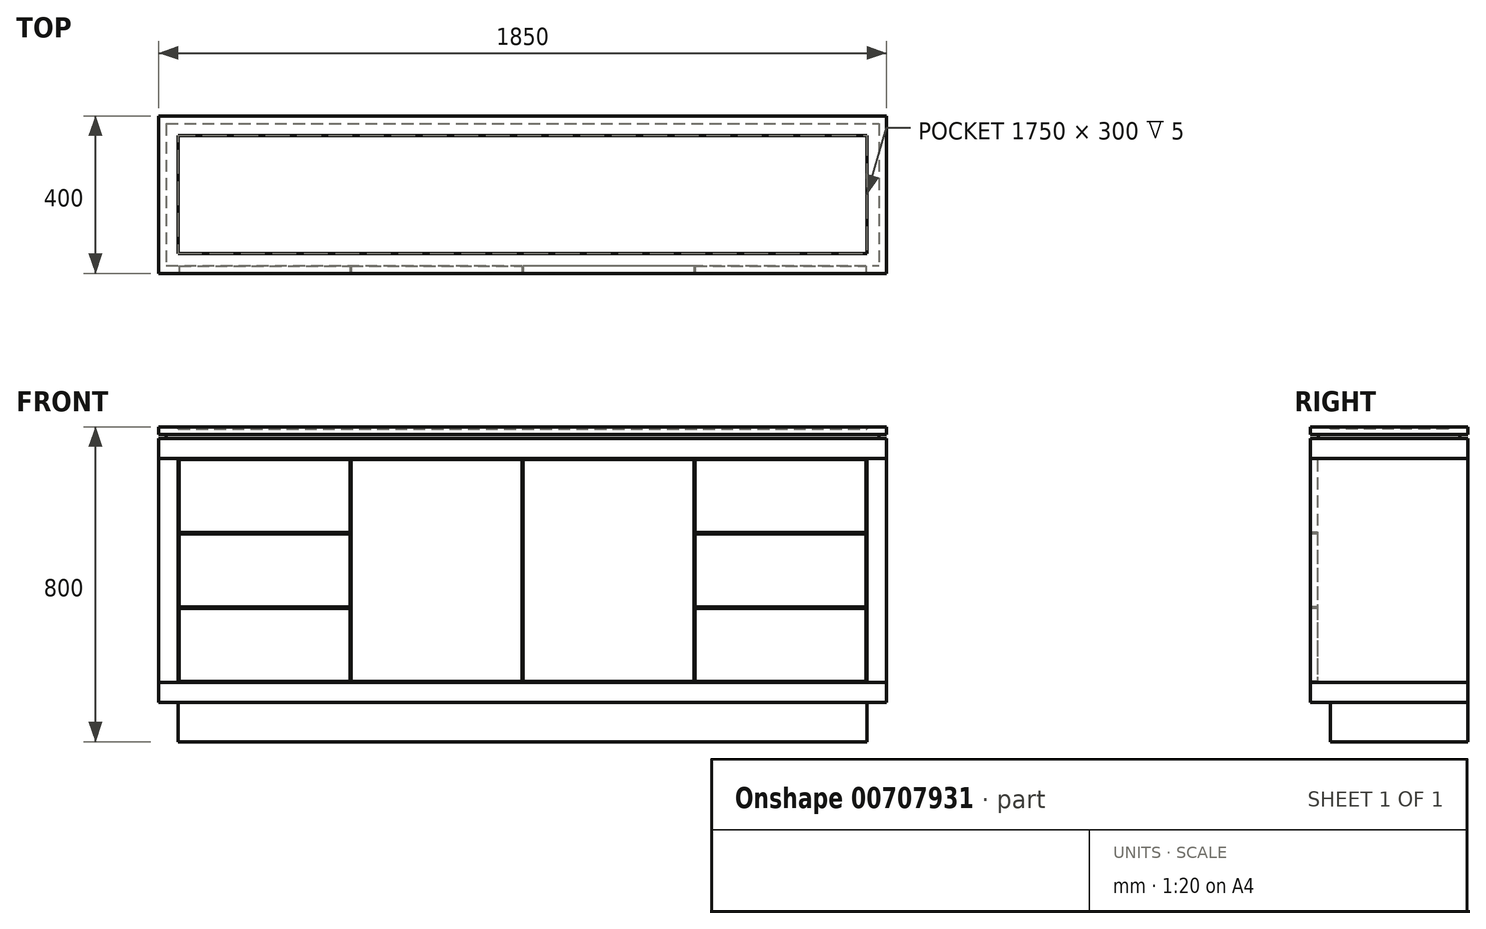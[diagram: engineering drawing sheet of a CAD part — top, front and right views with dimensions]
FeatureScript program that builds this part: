
annotation { "Feature Type Name" : "Feature", "Feature Type Description" : "" }
export const myFeature = defineFeature(function(context is Context, id is Id, definition is map)
    precondition{}
    {
        {
            var Q0;
            Q0=qCreatedBy(makeId("Front.planeOp"),FACE);
            var sketch = newSketch(context, id + "F0", { "sketchPlane" : qUnion([Q0])});
            skLineSegment(sketch, "E0.bottom", {"start": v(-925, 770) * mm, "end": v(925, 770) * mm});
            skLineSegment(sketch, "E0.top", {"start": v(-925, 100) * mm, "end": v(925, 100) * mm});
            skLineSegment(sketch, "E0.left", {"start": v(-925, 770) * mm, "end": v(-925, 100) * mm});
            skLineSegment(sketch, "E1.bottom", {"start": v(-925, 800) * mm, "end": v(925, 800) * mm});
            skLineSegment(sketch, "E1.top", {"start": v(-925, 780) * mm, "end": v(925, 780) * mm});
            skLineSegment(sketch, "E1.left", {"start": v(-925, 800) * mm, "end": v(-925, 780) * mm});
            skLineSegment(sketch, "E1.right", {"start": v(925, 800) * mm, "end": v(925, 780) * mm});
            skLineSegment(sketch, "E2", {"start": v(-875, 100) * mm, "end": v(-875, 0) * mm});
            skLineSegment(sketch, "E3", {"start": v(-875, 0) * mm, "end": v(875, 0) * mm});
            skLineSegment(sketch, "E4", {"start": v(875, 0) * mm, "end": v(875, 100) * mm});
            skLineSegment(sketch, "E5", {"start": v(905, 780) * mm, "end": v(905, 770) * mm});
            skLineSegment(sketch, "E6", {"start": v(925, 780) * mm, "end": v(925, 770) * mm, "construction": true});
            skLineSegment(sketch, "E7", {"start": v(-925, 780) * mm, "end": v(-925, 770) * mm, "construction": true});
            skLineSegment(sketch, "E8", {"start": v(-905, 770) * mm, "end": v(-905, 780) * mm});
            skLineSegment(sketch, "E9", {"start": v(925, 770) * mm, "end": v(925, 100) * mm});
            skLineSegment(sketch, "E10", {"start": v(925, 100) * mm, "end": v(925, 0) * mm, "construction": true});
            skLineSegment(sketch, "E11", {"start": v(925, 0) * mm, "end": v(875, 0) * mm, "construction": true});
            skLineSegment(sketch, "E12", {"start": v(-925, 100) * mm, "end": v(-925, 0) * mm, "construction": true});
            skLineSegment(sketch, "E13", {"start": v(-925, 0) * mm, "end": v(-875, 0) * mm, "construction": true});
            skLineSegment(sketch, "E14", {"start": v(-905, 775) * mm, "end": v(-925, 775) * mm, "construction": true});
            skLineSegment(sketch, "E15", {"start": v(925, 775) * mm, "end": v(905, 775) * mm, "construction": true});
            skLineSegment(sketch, "E16", {"start": v(-925, 720) * mm, "end": v(925, 720) * mm});
            skLineSegment(sketch, "E17", {"start": v(-925, 150) * mm, "end": v(925, 150) * mm});
            skLineSegment(sketch, "E18", {"start": v(-875, 100) * mm, "end": v(-875, 770) * mm});
            skLineSegment(sketch, "E19", {"start": v(875, 100) * mm, "end": v(875, 720) * mm});
            skLineSegment(sketch, "E20.bottom", {"start": v(-872, 528) * mm, "end": v(-438.25, 528) * mm});
            skLineSegment(sketch, "E20.top", {"start": v(-872, 153) * mm, "end": v(-438.25, 153) * mm});
            skLineSegment(sketch, "E20.left", {"start": v(-872, 528) * mm, "end": v(-872, 153) * mm});
            skLineSegment(sketch, "E20.right", {"start": v(-438.25, 528) * mm, "end": v(-438.25, 153) * mm});
            skLineSegment(sketch, "E21.bottom", {"start": v(-435.25, 528) * mm, "end": v(-1.5, 528) * mm});
            skLineSegment(sketch, "E21.top", {"start": v(-435.25, 153) * mm, "end": v(-1.5, 153) * mm});
            skLineSegment(sketch, "E21.left", {"start": v(-435.25, 528) * mm, "end": v(-435.25, 153) * mm});
            skLineSegment(sketch, "E21.right", {"start": v(-1.5, 528) * mm, "end": v(-1.5, 153) * mm});
            skLineSegment(sketch, "E22.bottom", {"start": v(1.5, 528) * mm, "end": v(435.25, 528) * mm});
            skLineSegment(sketch, "E22.top", {"start": v(1.5, 153) * mm, "end": v(435.25, 153) * mm});
            skLineSegment(sketch, "E22.left", {"start": v(1.5, 528) * mm, "end": v(1.5, 153) * mm});
            skLineSegment(sketch, "E22.right", {"start": v(435.25, 528) * mm, "end": v(435.25, 153) * mm});
            skLineSegment(sketch, "E23.bottom", {"start": v(438.25, 528) * mm, "end": v(872, 528) * mm});
            skLineSegment(sketch, "E23.top", {"start": v(438.25, 153) * mm, "end": v(872, 153) * mm});
            skLineSegment(sketch, "E23.left", {"start": v(438.25, 528) * mm, "end": v(438.25, 153) * mm});
            skLineSegment(sketch, "E23.right", {"start": v(872, 528) * mm, "end": v(872, 153) * mm});
            skLineSegment(sketch, "E24", {"start": v(-435.25, 153) * mm, "end": v(-438.25, 153) * mm, "construction": true});
            skLineSegment(sketch, "E25", {"start": v(-1.5, 153) * mm, "end": v(1.5, 153) * mm, "construction": true});
            skLineSegment(sketch, "E26", {"start": v(-872, 153) * mm, "end": v(-875, 153) * mm, "construction": true});
            skLineSegment(sketch, "E27", {"start": v(438.25, 153) * mm, "end": v(435.25, 153) * mm, "construction": true});
            skLineSegment(sketch, "E28", {"start": v(872, 153) * mm, "end": v(875, 153) * mm, "construction": true});
            skLineSegment(sketch, "E29", {"start": v(-872, 153) * mm, "end": v(-872, 150) * mm, "construction": true});
            skLineSegment(sketch, "E30", {"start": v(-655.12, 528) * mm, "end": v(-655.12, 531) * mm, "construction": true});
            skLineSegment(sketch, "E31", {"start": v(-655.12, 528) * mm, "end": v(-655.12, 340.5) * mm, "construction": true});
            skLineSegment(sketch, "E32", {"start": v(-655.12, 340.5) * mm, "end": v(-655.12, 153) * mm, "construction": true});
            skLineSegment(sketch, "E33", {"start": v(0, 532.5) * mm, "end": v(0, 720) * mm, "construction": true});
            skLineSegment(sketch, "E34", {"start": v(-435.25, 342) * mm, "end": v(435.25, 342) * mm});
            skLineSegment(sketch, "E35", {"start": v(435.25, 339) * mm, "end": v(-435.25, 339) * mm});
            skLineSegment(sketch, "E36", {"start": v(1.5, 528) * mm, "end": v(-1.5, 528) * mm, "construction": true});
            skLineSegment(sketch, "E37", {"start": v(0, 153) * mm, "end": v(0, 339) * mm, "construction": true});
            skLineSegment(sketch, "E38", {"start": v(0, 339) * mm, "end": v(0, 342) * mm, "construction": true});
            skLineSegment(sketch, "E39", {"start": v(0, 342) * mm, "end": v(0, 528) * mm, "construction": true});
            skLineSegment(sketch, "E40", {"start": v(-435.25, 342) * mm, "end": v(-872, 342) * mm});
            skLineSegment(sketch, "E41", {"start": v(-435.25, 339) * mm, "end": v(-872, 339) * mm});
            skLineSegment(sketch, "E42", {"start": v(435.25, 342) * mm, "end": v(872, 342) * mm});
            skLineSegment(sketch, "E43", {"start": v(435.25, 339) * mm, "end": v(872, 339) * mm});
            skPoint(sketch, "E44.endSnap0", {"position": v(0, 800) * mm});
            skLineSegment(sketch, "E45.bottom", {"start": v(-872, 717) * mm, "end": v(-438.25, 717) * mm});
            skLineSegment(sketch, "E45.top", {"start": v(-872, 531) * mm, "end": v(-438.25, 531) * mm});
            skLineSegment(sketch, "E45.left", {"start": v(-872, 717) * mm, "end": v(-872, 531) * mm});
            skLineSegment(sketch, "E45.right", {"start": v(-438.25, 717) * mm, "end": v(-438.25, 531) * mm});
            skLineSegment(sketch, "E46.bottom", {"start": v(-435.25, 717) * mm, "end": v(-1.5, 717) * mm});
            skLineSegment(sketch, "E46.top", {"start": v(-435.25, 531) * mm, "end": v(-1.5, 531) * mm});
            skLineSegment(sketch, "E46.left", {"start": v(-435.25, 717) * mm, "end": v(-435.25, 531) * mm});
            skLineSegment(sketch, "E46.right", {"start": v(-1.5, 717) * mm, "end": v(-1.5, 531) * mm});
            skLineSegment(sketch, "E47", {"start": v(-872, 531) * mm, "end": v(-872, 528) * mm});
            skLineSegment(sketch, "E48", {"start": v(-872, 717) * mm, "end": v(-872, 720) * mm});
            skLineSegment(sketch, "E49", {"start": v(-435.25, 531) * mm, "end": v(-435.25, 528) * mm});
            skLineSegment(sketch, "E50", {"start": v(-438.25, 717) * mm, "end": v(-435.25, 717) * mm});
            skLineSegment(sketch, "E51", {"start": v(-1.5, 531) * mm, "end": v(-1.5, 528) * mm});
            skSolve(sketch);
        }
        {
            var Q0;
            {var subQ5=sQuery(id+"F0.wireOp",EDGE,"E0.bottom");var subQ7=makeQuery(id+"F0.imprint","INTERSECT",VERTEX,{"derivedFrom":[subQ5,sQuery(id+"F0.wireOp",EDGE,"E5")]});Q0=makeQuery(id+"F0.imprint","IMPRINT",FACE,{"disambiguationData":[TD([[makeQuery(id+"F0.imprint","IMPRINT",EDGE,{"disambiguationData":[TD([[subQ7,1.0]])],"derivedFrom":subQ5}),-1.0]])]});}
            var Q1;
            {var subQ1=sQuery(id+"F0.wireOp",EDGE,"E0.left");var subQ5=sQuery(id+"F0.wireOp",EDGE,"E0.bottom");var subQ6=makeQuery(id+"F0.imprint","INTERSECT",VERTEX,{"derivedFrom":[subQ5,subQ1]});Q1=makeQuery(id+"F0.imprint","IMPRINT",FACE,{"disambiguationData":[TD([[makeQuery(id+"F0.imprint","IMPRINT",EDGE,{"disambiguationData":[TD([[subQ6,-1.0]])],"derivedFrom":subQ5}),-1.0]])]});}
            var Q2;
            {var subQ0=sQuery(id+"F0.wireOp",EDGE,"E0.left");var subQ1=sQuery(id+"F0.wireOp",EDGE,"E0.top");var subQ2=makeQuery(id+"F0.imprint","INTERSECT",VERTEX,{"derivedFrom":[subQ1,subQ0]});Q2=makeQuery(id+"F0.imprint","IMPRINT",FACE,{"disambiguationData":[TD([[makeQuery(id+"F0.imprint","IMPRINT",EDGE,{"disambiguationData":[TD([[subQ2,1.0]])],"derivedFrom":subQ0}),1.0]])]});}
            var Q3;
            {var subQ0=sQuery(id+"F0.wireOp",EDGE,"E18");var subQ5=sQuery(id+"F0.wireOp",EDGE,"E17");var subQ6=makeQuery(id+"F0.imprint","INTERSECT",VERTEX,{"derivedFrom":[subQ5,subQ0]});Q3=makeQuery(id+"F0.imprint","IMPRINT",FACE,{"disambiguationData":[TD([[makeQuery(id+"F0.imprint","IMPRINT",EDGE,{"disambiguationData":[TD([[subQ6,-1.0]])],"derivedFrom":subQ5}),-1.0]])]});}
            var Q4;
            {var subQ0=sQuery(id+"F0.wireOp",EDGE,"E9");var subQ1=sQuery(id+"F0.wireOp",EDGE,"E0.top");var subQ2=makeQuery(id+"F0.imprint","INTERSECT",VERTEX,{"derivedFrom":[subQ1,subQ0]});Q4=makeQuery(id+"F0.imprint","IMPRINT",FACE,{"disambiguationData":[TD([[makeQuery(id+"F0.imprint","IMPRINT",EDGE,{"disambiguationData":[TD([[subQ2,1.0]])],"derivedFrom":subQ0}),-1.0]])]});}
            var Q5;
            Q5=makeQuery(id+"F0.imprint","IMPRINT",FACE,{"disambiguationData":[TD([[makeQuery(id+"F0.imprint","IMPRINT",EDGE,{"derivedFrom":sQuery(id+"F0.wireOp",EDGE,"5v0JZrxY-nqoR-NWn2-a046-kkwBJGH1RzHE.bottom")}),-1.0]])]});
            extrude(context, id + "F1", {"entities" : qUnion([Q0, Q1, Q2, Q3, Q4, Q5]), "oppositeDirection" : true, "depth" : 400 * mm, "offsetDistance" : 25 * mm});
        }
        {
            var Q0;
            {var subQ0=sQuery(id+"F0.wireOp",EDGE,"5v0JZrxY-nqoR-NWn2-a046-kkwBJGH1RzHE.left");Q0=makeQuery(id+"F0.imprint","IMPRINT",FACE,{"disambiguationData":[TD([[makeQuery(id+"F0.imprint","IMPRINT",EDGE,{"derivedFrom":subQ0}),-1.0]])]});}
            var Q1;
            {var subQ0=sQuery(id+"F0.wireOp",EDGE,"5v0JZrxY-nqoR-NWn2-a046-kkwBJGH1RzHE.right");Q1=makeQuery(id+"F0.imprint","IMPRINT",FACE,{"disambiguationData":[TD([[makeQuery(id+"F0.imprint","IMPRINT",EDGE,{"derivedFrom":subQ0}),1.0]])]});}
            var Q2;
            {var subQ0=sQuery(id+"F0.wireOp",EDGE,"E16");var subQ1=sQuery(id+"F0.wireOp",EDGE,"E0.left");var subQ2=makeQuery(id+"F0.imprint","INTERSECT",VERTEX,{"derivedFrom":[subQ1,subQ0]});Q2=makeQuery(id+"F0.imprint","IMPRINT",FACE,{"disambiguationData":[TD([[makeQuery(id+"F0.imprint","IMPRINT",EDGE,{"disambiguationData":[TD([[subQ2,-1.0]])],"derivedFrom":subQ1}),1.0]])]});}
            var Q3;
            {var subQ0=sQuery(id+"F0.wireOp",EDGE,"E16");var subQ1=sQuery(id+"F0.wireOp",EDGE,"E9");var subQ2=makeQuery(id+"F0.imprint","INTERSECT",VERTEX,{"derivedFrom":[subQ1,subQ0]});Q3=makeQuery(id+"F0.imprint","IMPRINT",FACE,{"disambiguationData":[TD([[makeQuery(id+"F0.imprint","IMPRINT",EDGE,{"disambiguationData":[TD([[subQ2,-1.0]])],"derivedFrom":subQ1}),-1.0]])]});}
            extrude(context, id + "F2", {"entities" : qUnion([Q0, Q1, Q2, Q3]), "oppositeDirection" : true, "depth" : 400 * mm, "offsetDistance" : 25 * mm});
        }
        {
            var Q0;
            {var subQ0=sQuery(id+"F0.wireOp",EDGE,"E2");Q0=makeQuery(id+"F0.imprint","IMPRINT",FACE,{"disambiguationData":[TD([[makeQuery(id+"F0.imprint","IMPRINT",EDGE,{"derivedFrom":subQ0}),1.0]])]});}
            extrude(context, id + "F3", {"entities" : qUnion([Q0]), "oppositeDirection" : true, "depth" : 400 * mm, "offsetDistance" : 25 * mm, "hasSecondDirection" : true, "secondDirectionOppositeDirection" : true, "secondDirectionDepth" : 50 * mm});
        }
        {
            var Q0;
            {var subQ0=sQuery(id+"F0.wireOp",EDGE,"E20.bottom");Q0=makeQuery(id+"F0.imprint","IMPRINT",FACE,{"disambiguationData":[TD([[makeQuery(id+"F0.imprint","IMPRINT",EDGE,{"derivedFrom":subQ0}),-1.0]])]});}
            var Q1;
            {var subQ0=sQuery(id+"F0.wireOp",EDGE,"E20.top");Q1=makeQuery(id+"F0.imprint","IMPRINT",FACE,{"disambiguationData":[TD([[makeQuery(id+"F0.imprint","IMPRINT",EDGE,{"derivedFrom":subQ0}),1.0]])]});}
            var Q2;
            {var subQ0=sQuery(id+"F0.wireOp",EDGE,"E21.bottom");Q2=makeQuery(id+"F0.imprint","IMPRINT",FACE,{"disambiguationData":[TD([[makeQuery(id+"F0.imprint","IMPRINT",EDGE,{"derivedFrom":subQ0}),-1.0]])]});}
            var Q3;
            {var subQ0=sQuery(id+"F0.wireOp",EDGE,"E21.top");Q3=makeQuery(id+"F0.imprint","IMPRINT",FACE,{"disambiguationData":[TD([[makeQuery(id+"F0.imprint","IMPRINT",EDGE,{"derivedFrom":subQ0}),1.0]])]});}
            var Q4;
            {var subQ0=sQuery(id+"F0.wireOp",EDGE,"E34");var subQ5=sQuery(id+"F0.wireOp",EDGE,"E21.right");var subQ6=makeQuery(id+"F0.imprint","INTERSECT",VERTEX,{"derivedFrom":[subQ5,subQ0]});Q4=makeQuery(id+"F0.imprint","IMPRINT",FACE,{"disambiguationData":[TD([[makeQuery(id+"F0.imprint","IMPRINT",EDGE,{"disambiguationData":[TD([[subQ6,-1.0]])],"derivedFrom":subQ5}),-1.0]])]});}
            var Q5;
            Q5=makeQuery(id+"F0.imprint","IMPRINT",FACE,{"disambiguationData":[TD([[makeQuery(id+"F0.imprint","IMPRINT",EDGE,{"derivedFrom":sQuery(id+"F0.wireOp",EDGE,"E45.bottom")}),-1.0]])]});
            var Q6;
            Q6=makeQuery(id+"F0.imprint","IMPRINT",FACE,{"disambiguationData":[TD([[makeQuery(id+"F0.imprint","IMPRINT",EDGE,{"derivedFrom":sQuery(id+"F0.wireOp",EDGE,"E46.bottom")}),-1.0]])]});
            var Q7;
            Q7=makeQuery(id+"F0.imprint","IMPRINT",FACE,{"disambiguationData":[TD([[makeQuery(id+"F0.imprint","IMPRINT",EDGE,{"derivedFrom":sQuery(id+"F0.wireOp",EDGE,"E21.bottom")}),1.0]])]});
            extrude(context, id + "F4", {"entities" : qUnion([Q0, Q1, Q2, Q3, Q4, Q5, Q6, Q7]), "oppositeDirection" : true, "depth" : 18 * mm, "offsetDistance" : 25 * mm});
        }
        {
            var Q0;
            {var subQ0=sQuery(id+"F0.wireOp",EDGE,"E5");Q0=makeQuery(id+"F0.imprint","IMPRINT",FACE,{"disambiguationData":[TD([[makeQuery(id+"F0.imprint","IMPRINT",EDGE,{"derivedFrom":subQ0}),-1.0]])]});}
            extrude(context, id + "F5", {"entities" : qUnion([Q0]), "oppositeDirection" : true, "depth" : 380 * mm, "offsetDistance" : 25 * mm, "hasSecondDirection" : true, "secondDirectionOppositeDirection" : true, "secondDirectionDepth" : 20 * mm});
        }
        {
            var Q0;
            Q0=makeQuery(id+"F0.imprint","IMPRINT",FACE,{"disambiguationData":[TD([[makeQuery(id+"F0.imprint","IMPRINT",EDGE,{"derivedFrom":sQuery(id+"F0.wireOp",EDGE,"E1.bottom")}),-1.0]])]});
            extrude(context, id + "F6", {"entities" : qUnion([Q0]), "oppositeDirection" : true, "depth" : 400 * mm, "offsetDistance" : 25 * mm});
        }
        {
            var Q0;
            Q0=makeQuery(id+"F4.opExtrude","SWEPT_FACE",FACE,{"disambiguationData":[OSD([sQuery(id+"F0.wireOp",EDGE,"E21.right"),sQuery(id+"F0.wireOp",EDGE,"E46.right"),sQuery(id+"F0.wireOp",EDGE,"E51")])]});
            cPlane(context, id + "F7", {"entities" : qUnion([Q0]), "cplaneType" : CPlaneType.OFFSET, "offset" : 1.5 * mm, "width" : 150 * mm, "height" : 150 * mm});
        }
        {
            var Q0;
            Q0=makeQuery(id+"F4.opExtrude","SWEPT_BODY",BODY,{"disambiguationData":[OSD([sQuery(id+"F0.wireOp",EDGE,"E45.bottom"),sQuery(id+"F0.wireOp",EDGE,"E45.top"),sQuery(id+"F0.wireOp",EDGE,"E45.left"),sQuery(id+"F0.wireOp",EDGE,"E45.right")])]});
            var Q1;
            Q1=makeQuery(id+"F4.opExtrude","SWEPT_BODY",BODY,{"disambiguationData":[OSD([sQuery(id+"F0.wireOp",EDGE,"E20.bottom"),sQuery(id+"F0.wireOp",EDGE,"E20.left"),sQuery(id+"F0.wireOp",EDGE,"E20.right"),sQuery(id+"F0.wireOp",EDGE,"E40")])]});
            var Q2;
            Q2=makeQuery(id+"F4.opExtrude","SWEPT_BODY",BODY,{"disambiguationData":[OSD([sQuery(id+"F0.wireOp",EDGE,"E20.top"),sQuery(id+"F0.wireOp",EDGE,"E20.left"),sQuery(id+"F0.wireOp",EDGE,"E20.right"),sQuery(id+"F0.wireOp",EDGE,"E41")])]});
            var Q3;
            Q3=makeQuery(id+"F4.opExtrude","SWEPT_BODY",BODY,{"disambiguationData":[OSD([sQuery(id+"F0.wireOp",EDGE,"E21.top"),sQuery(id+"F0.wireOp",EDGE,"E21.left"),sQuery(id+"F0.wireOp",EDGE,"E21.right"),sQuery(id+"F0.wireOp",EDGE,"E46.bottom"),sQuery(id+"F0.wireOp",EDGE,"E46.left"),sQuery(id+"F0.wireOp",EDGE,"E46.right"),sQuery(id+"F0.wireOp",EDGE,"E49"),sQuery(id+"F0.wireOp",EDGE,"E51")])]});
            var Q4;
            Q4=qCreatedBy(id+"F7.planeOp",FACE);
            mirror(context, id + "F8", {"entities" : qUnion([Q0, Q1, Q2, Q3]), "mirrorPlane" : qUnion([Q4])});
        }
        {
            var Q0;
            Q0=makeQuery(id+"F6.opExtrude","SWEPT_FACE",FACE,{"disambiguationData":[OSD([sQuery(id+"F0.wireOp",EDGE,"E1.bottom")])]});
            var sketch = newSketch(context, id + "F9", { "sketchPlane" : qUnion([Q0])});
            skLineSegment(sketch, "E52.bottom", {"start": v(-875, 350) * mm, "end": v(875, 350) * mm});
            skLineSegment(sketch, "E52.top", {"start": v(-875, 50) * mm, "end": v(875, 50) * mm});
            skLineSegment(sketch, "E52.left", {"start": v(-875, 350) * mm, "end": v(-875, 50) * mm});
            skLineSegment(sketch, "E52.right", {"start": v(875, 350) * mm, "end": v(875, 50) * mm});
            skSolve(sketch);
        }
        {
            var Q0;
            Q0=makeQuery(id+"F9.imprint","IMPRINT",FACE,{"disambiguationData":[TD([[makeQuery(id+"F9.imprint","IMPRINT",EDGE,{"derivedFrom":sQuery(id+"F9.wireOp",EDGE,"E52.bottom")}),-1.0]])]});
            extrude(context, id + "F10", {"entities" : qUnion([Q0]), "operationType" : NewBodyOperationType.REMOVE, "oppositeDirection" : true, "depth" : 5 * mm, "offsetDistance" : 25 * mm});
        }
        {
            var Q0;
            Q0=makeQuery(id+"F10.boolean.opBoolean","COPY",FACE,{"derivedFrom":makeQuery(id+"F10.opExtrude","CAP_FACE",FACE,{"disambiguationData":[OSD([sQuery(id+"F9.wireOp",EDGE,"E52.bottom"),sQuery(id+"F9.wireOp",EDGE,"E52.top"),sQuery(id+"F9.wireOp",EDGE,"E52.left"),sQuery(id+"F9.wireOp",EDGE,"E52.right")])],"isStart":false})});
            extrude(context, id + "F11", {"entities" : qUnion([Q0]), "depth" : 3 * mm, "offsetDistance" : 25 * mm});
        }
        {
            var Q0;
            Q0=makeQuery(id+"F11.opExtrude","CAP_FACE",FACE,{"disambiguationData":[OSD([sQuery(id+"F9.wireOp",EDGE,"E52.bottom"),sQuery(id+"F9.wireOp",EDGE,"E52.top"),sQuery(id+"F9.wireOp",EDGE,"E52.left"),sQuery(id+"F9.wireOp",EDGE,"E52.right")])],"isStart":false});
            extrude(context, id + "F12", {"entities" : qUnion([Q0]), "depth" : 2 * mm, "offsetDistance" : 25 * mm});
        }
    });
